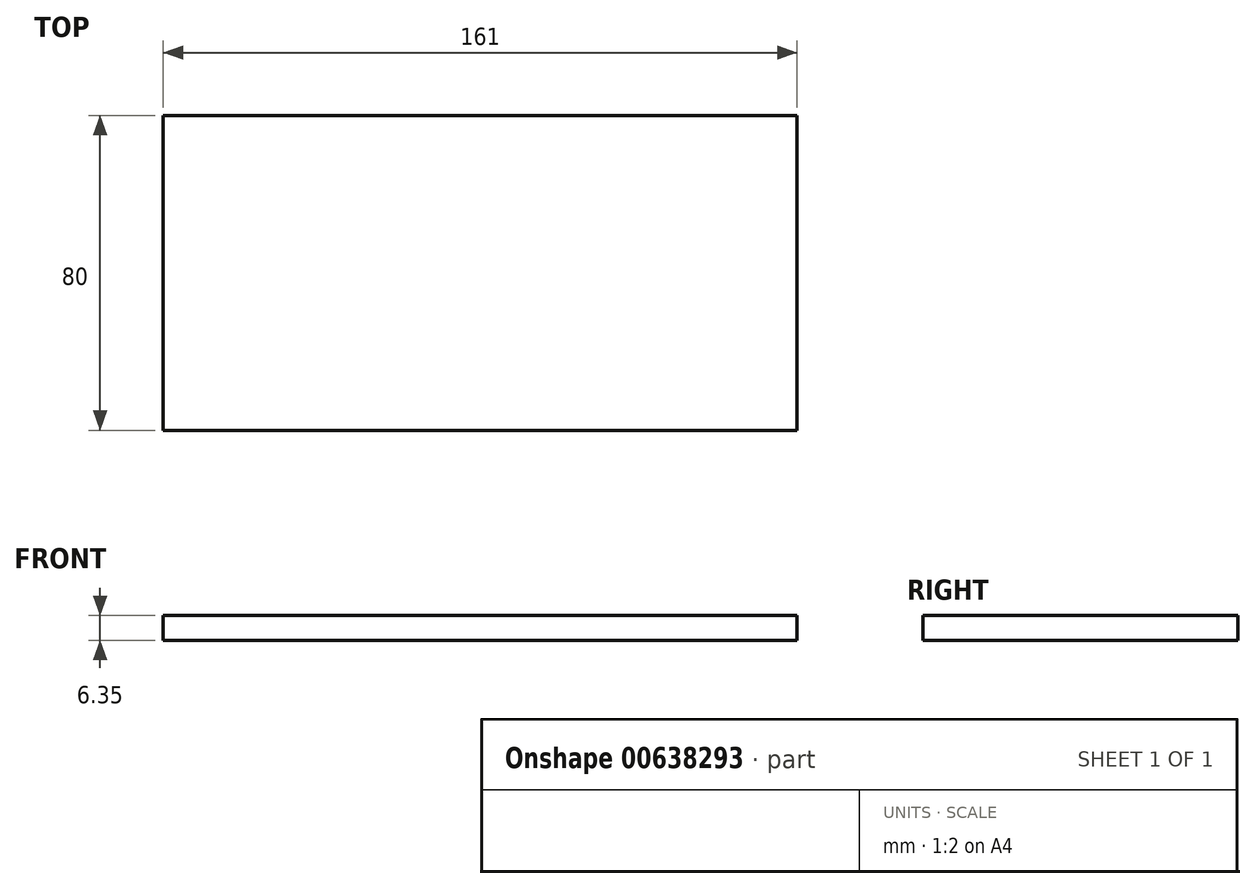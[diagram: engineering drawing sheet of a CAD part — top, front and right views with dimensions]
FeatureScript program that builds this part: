
annotation { "Feature Type Name" : "Feature", "Feature Type Description" : "" }
export const myFeature = defineFeature(function(context is Context, id is Id, definition is map)
    precondition{}
    {
        {
            var Q0;
            Q0=qCreatedBy(makeId("Top.planeOp"),FACE);
            var sketch = newSketch(context, id + "F0", { "sketchPlane" : qUnion([Q0])});
            skLineSegment(sketch, "E0.bottom", {"start": v(0, 0) * mm, "end": v(161, 0) * mm});
            skLineSegment(sketch, "E0.top", {"start": v(0, -80) * mm, "end": v(161, -80) * mm});
            skLineSegment(sketch, "E0.left", {"start": v(0, 0) * mm, "end": v(0, -80) * mm});
            skLineSegment(sketch, "E0.right", {"start": v(161, 0) * mm, "end": v(161, -80) * mm});
            skSolve(sketch);
        }
        {
            var Q0;
            Q0=makeQuery(id+"F0.imprint","IMPRINT",FACE,{"disambiguationData":[TD([[makeQuery(id+"F0.imprint","IMPRINT",EDGE,{"derivedFrom":sQuery(id+"F0.wireOp",EDGE,"E0.bottom")}),-1.0]])]});
            extrude(context, id + "F1", {"entities" : qUnion([Q0]), "depth" : 6.35 * mm, "offsetDistance" : 25.4 * mm});
        }
    });
